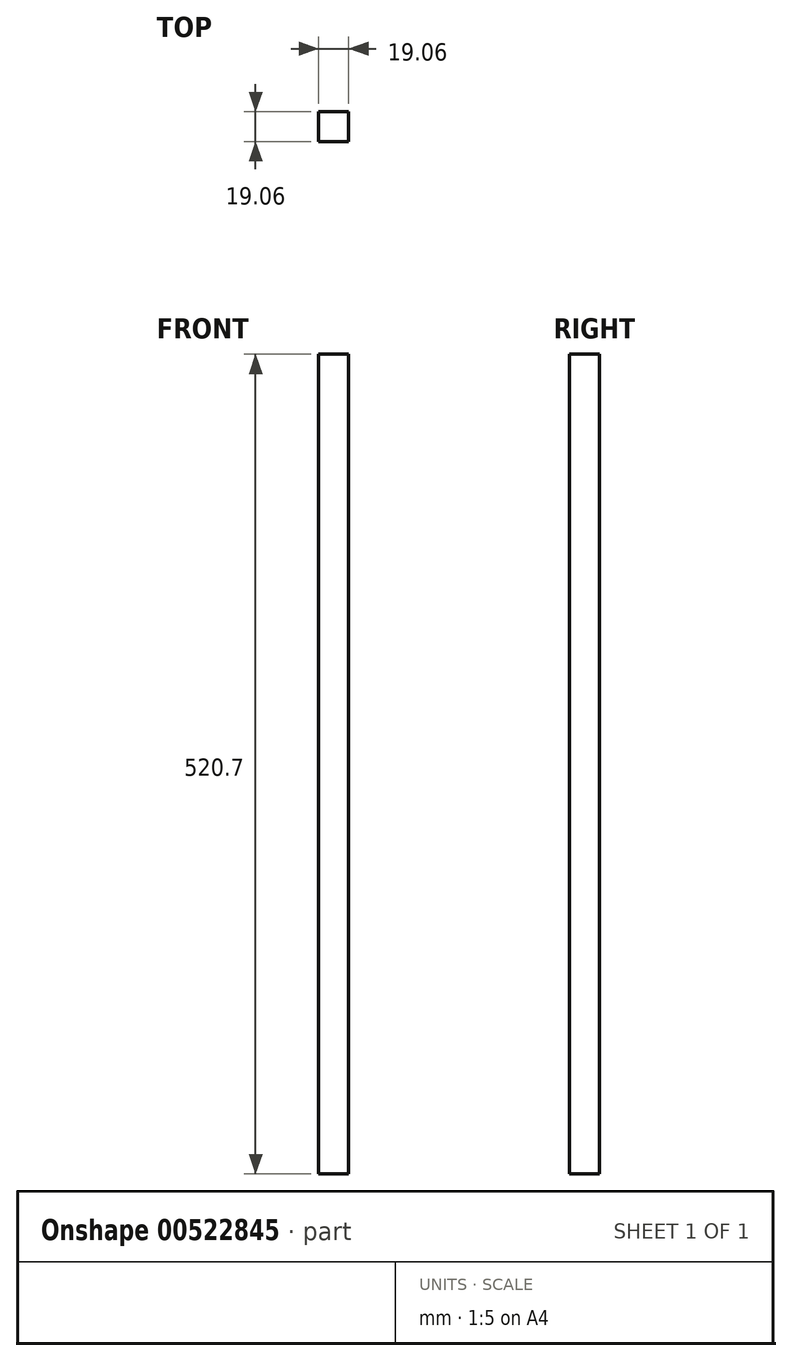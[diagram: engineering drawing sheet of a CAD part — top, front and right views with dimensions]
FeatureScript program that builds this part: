
annotation { "Feature Type Name" : "Feature", "Feature Type Description" : "" }
export const myFeature = defineFeature(function(context is Context, id is Id, definition is map)
    precondition{}
    {
        {
            var Q0;
            Q0=qCreatedBy(makeId("Top.planeOp"),FACE);
            var sketch = newSketch(context, id + "F0", { "sketchPlane" : qUnion([Q0])});
            skLineSegment(sketch, "E0.bottom", {"start": v(-9.52, 9.53) * mm, "end": v(9.53, 9.53) * mm});
            skLineSegment(sketch, "E0.top", {"start": v(-9.53, -9.52) * mm, "end": v(9.53, -9.52) * mm});
            skLineSegment(sketch, "E0.left", {"start": v(-9.52, 9.53) * mm, "end": v(-9.53, -9.52) * mm});
            skLineSegment(sketch, "E0.right", {"start": v(9.53, 9.53) * mm, "end": v(9.53, -9.52) * mm});
            skPoint(sketch, "E0.middle", {"position": v(0, 0) * mm});
            skSolve(sketch);
        }
        {
            var Q0;
            Q0=makeQuery(id+"F0.imprint","IMPRINT",FACE,{"disambiguationData":[TD([[makeQuery(id+"F0.imprint","IMPRINT",EDGE,{"derivedFrom":sQuery(id+"F0.wireOp",EDGE,"E0.bottom")}),-1.0]])]});
            extrude(context, id + "F1", {"entities" : qUnion([Q0]), "depth" : 520.7 * mm, "offsetDistance" : 25.4 * mm});
        }
    });
